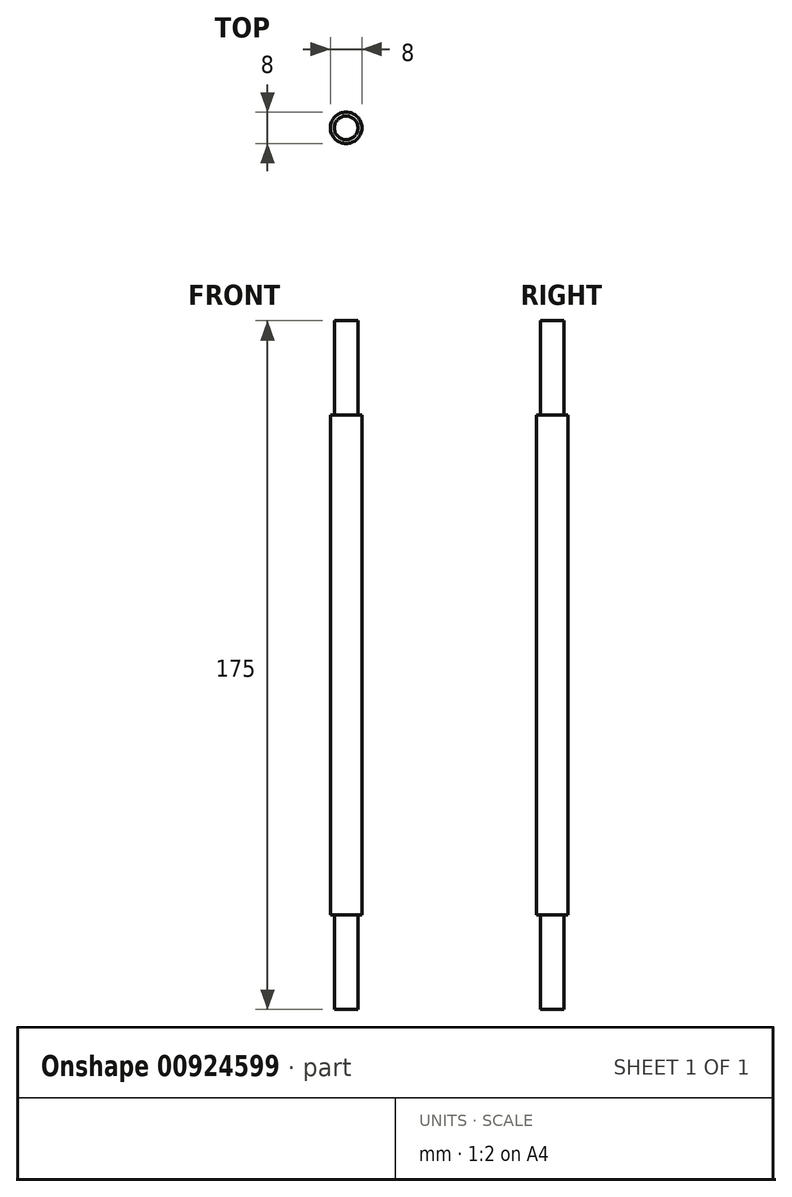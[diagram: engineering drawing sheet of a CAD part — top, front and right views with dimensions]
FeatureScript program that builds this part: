
annotation { "Feature Type Name" : "Feature", "Feature Type Description" : "" }
export const myFeature = defineFeature(function(context is Context, id is Id, definition is map)
    precondition{}
    {
        {
            var Q0;
            Q0=qCreatedBy(makeId("Front.planeOp"),FACE);
            var sketch = newSketch(context, id + "F0", { "sketchPlane" : qUnion([Q0])});
            skLineSegment(sketch, "E0", {"start": v(0, 107) * mm, "end": v(-3, 107) * mm});
            skLineSegment(sketch, "E1", {"start": v(-3, 107) * mm, "end": v(-3, 92) * mm});
            skLineSegment(sketch, "E2", {"start": v(-3, 92) * mm, "end": v(-4, 92) * mm});
            skLineSegment(sketch, "E3", {"start": v(-4, 92) * mm, "end": v(-4, -35) * mm});
            skLineSegment(sketch, "E4", {"start": v(-4, -35) * mm, "end": v(-3, -35) * mm});
            skLineSegment(sketch, "E5", {"start": v(-3, -35) * mm, "end": v(-3, -50) * mm});
            skLineSegment(sketch, "E6", {"start": v(-3, -50) * mm, "end": v(0, -50) * mm});
            skLineSegment(sketch, "E7", {"start": v(0, -50) * mm, "end": v(0, 107) * mm});
            skLineSegment(sketch, "E8", {"start": v(0, 60) * mm, "end": v(0, -60) * mm, "construction": true});
            skSolve(sketch);
        }
        {
            var Q0;
            Q0=makeQuery(id+"F0.imprint","IMPRINT",FACE,{"disambiguationData":[TD([[makeQuery(id+"F0.imprint","IMPRINT",EDGE,{"derivedFrom":sQuery(id+"F0.wireOp",EDGE,"E0")}),1.0]])]});
            var Q1;
            Q1=sQuery(id+"F0.wireOp",EDGE,"E8");
            revolve(context, id + "F1", {"surfaceOperationType" : NewSurfaceOperationType.NEW, "entities" : qUnion([Q0]), "axis" : qUnion([Q1]), "revolveType" : RevolveType.FULL});
        }
        {
            var Q0;
            Q0=makeQuery(id+"F1.opRevolve","SWEPT_FACE",FACE,{"disambiguationData":[OSD([sQuery(id+"F0.wireOp",EDGE,"E0")])]});
            extrude(context, id + "F2", {"entities" : qUnion([Q0]), "operationType" : NewBodyOperationType.ADD, "depth" : 9 * mm, "offsetDistance" : 25 * mm});
        }
        {
            var Q0;
            Q0=makeQuery(id+"F1.opRevolve","SWEPT_FACE",FACE,{"disambiguationData":[OSD([sQuery(id+"F0.wireOp",EDGE,"E6")])]});
            extrude(context, id + "F3", {"entities" : qUnion([Q0]), "operationType" : NewBodyOperationType.ADD, "depth" : 9 * mm, "offsetDistance" : 25 * mm});
        }
    });
